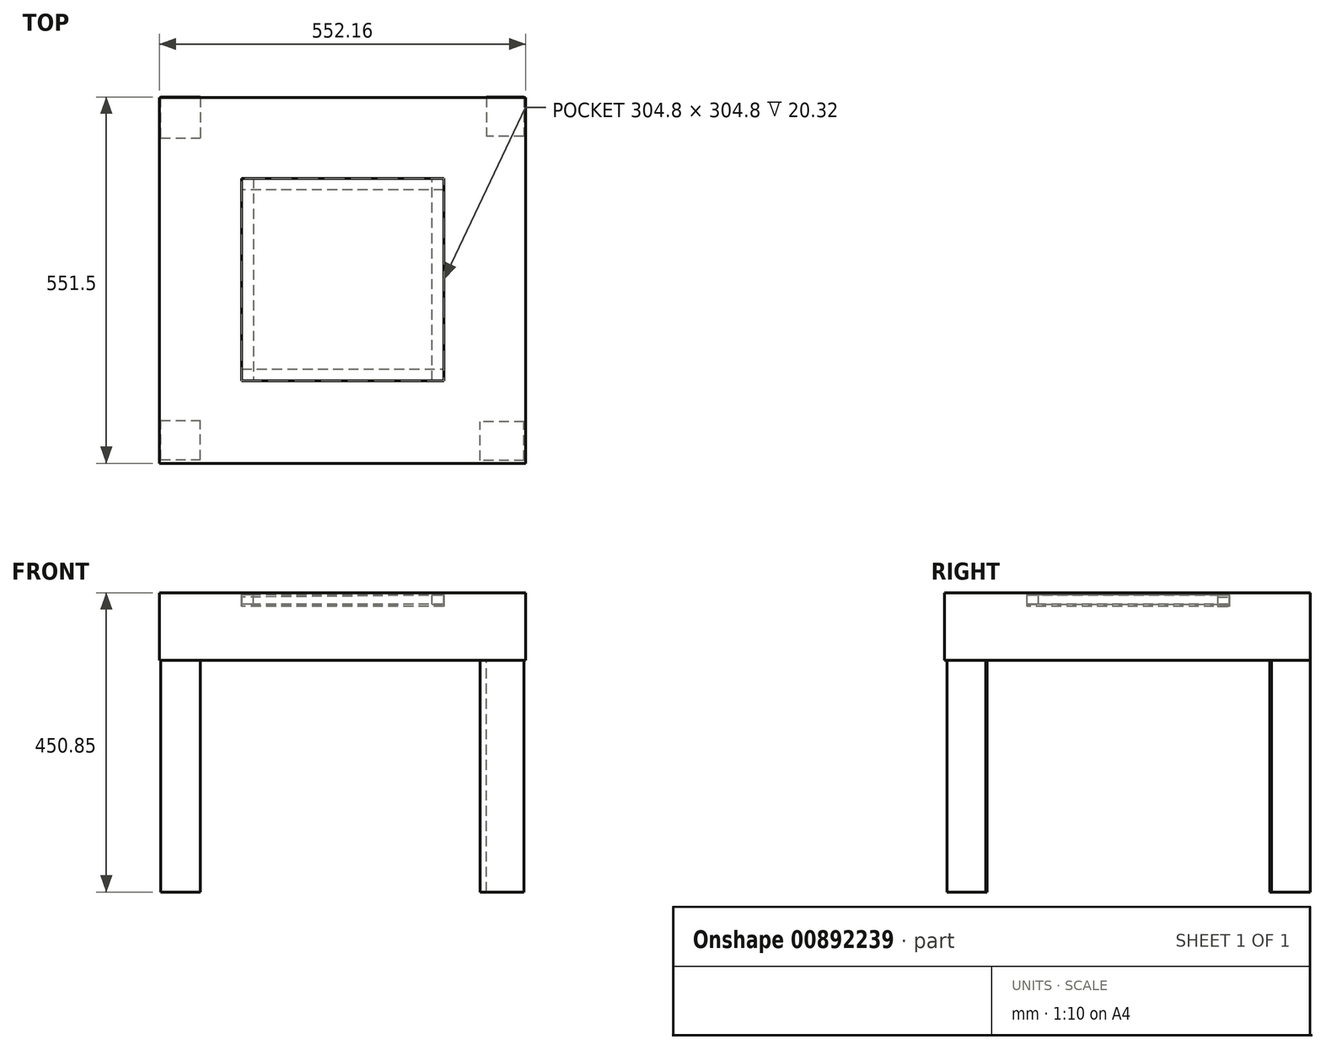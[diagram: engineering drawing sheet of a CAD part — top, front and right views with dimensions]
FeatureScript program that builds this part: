
annotation { "Feature Type Name" : "Feature", "Feature Type Description" : "" }
export const myFeature = defineFeature(function(context is Context, id is Id, definition is map)
    precondition{}
    {
        {
            var Q0;
            Q0=qCreatedBy(makeId("Top.planeOp"),FACE);
            var sketch = newSketch(context, id + "F0", { "sketchPlane" : qUnion([Q0])});
            skLineSegment(sketch, "E0.bottom", {"start": v(274.64, -274.64) * mm, "end": v(-274.64, -274.64) * mm});
            skLineSegment(sketch, "E0.top", {"start": v(274.64, 274.64) * mm, "end": v(-274.64, 274.64) * mm});
            skLineSegment(sketch, "E0.left", {"start": v(274.64, -274.64) * mm, "end": v(274.64, 274.64) * mm});
            skLineSegment(sketch, "E0.right", {"start": v(-274.64, -274.64) * mm, "end": v(-274.64, 274.64) * mm});
            skPoint(sketch, "E0.middle", {"position": v(0, 0) * mm});
            skSolve(sketch);
        }
        {
            var Q0;
            Q0=qCreatedBy(makeId("Front.planeOp"),FACE);
            var sketch = newSketch(context, id + "F1", { "sketchPlane" : qUnion([Q0])});
            skLineSegment(sketch, "E1.bottom", {"start": v(-276.39, 0) * mm, "end": v(275.77, 0) * mm});
            skLineSegment(sketch, "E1.top", {"start": v(-276.39, 101.6) * mm, "end": v(275.77, 101.6) * mm});
            skLineSegment(sketch, "E1.left", {"start": v(-276.39, 0) * mm, "end": v(-276.39, 101.6) * mm});
            skLineSegment(sketch, "E1.right", {"start": v(275.77, 0) * mm, "end": v(275.77, 101.6) * mm});
            skSolve(sketch);
        }
        {
            var Q0;
            Q0 = qSketchRegion(id + "F1", true);
            extrude(context, id + "F2", {"entities" : qUnion([Q0]), "depth" : 276.86 * mm, "offsetDistance" : 25.4 * mm});
        }
        {
            var Q0;
            Q0=makeQuery(id+"F1.imprint","IMPRINT",FACE,{"disambiguationData":[TD([[makeQuery(id+"F1.imprint","IMPRINT",EDGE,{"derivedFrom":sQuery(id+"F1.wireOp",EDGE,"E1.bottom")}),1.0]])]});
            extrude(context, id + "F3", {"entities" : qUnion([Q0]), "oppositeDirection" : true, "depth" : 274.32 * mm, "offsetDistance" : 25.4 * mm});
        }
        {
            var Q0;
            Q0=makeQuery(id+"F3.opExtrude","SWEPT_FACE",FACE,{"disambiguationData":[OSD([sQuery(id+"F1.wireOp",EDGE,"E1.top")])]});
            var sketch = newSketch(context, id + "F4", { "sketchPlane" : qUnion([Q0])});
            skLineSegment(sketch, "E2.bottom", {"start": v(152.4, 152.4) * mm, "end": v(-152.4, 152.4) * mm});
            skLineSegment(sketch, "E2.top", {"start": v(152.4, -152.4) * mm, "end": v(-152.4, -152.4) * mm});
            skLineSegment(sketch, "E2.left", {"start": v(152.4, 152.4) * mm, "end": v(152.4, -152.4) * mm});
            skLineSegment(sketch, "E2.right", {"start": v(-152.4, 152.4) * mm, "end": v(-152.4, -152.4) * mm});
            skPoint(sketch, "E2.middle", {"position": v(0, 0) * mm});
            skSolve(sketch);
        }
        {
            var Q0;
            Q0 = qSketchRegion(id + "F4", true);
            extrude(context, id + "F5", {"entities" : qUnion([Q0]), "operationType" : NewBodyOperationType.REMOVE, "oppositeDirection" : true, "depth" : 20.32 * mm, "offsetDistance" : 25.4 * mm});
        }
        {
            var Q0;
            Q0=makeQuery(id+"F2.opExtrude","SWEPT_BODY",BODY,{"disambiguationData":[OSD([sQuery(id+"F1.wireOp",EDGE,"E1.bottom"),sQuery(id+"F1.wireOp",EDGE,"E1.top"),sQuery(id+"F1.wireOp",EDGE,"E1.left"),sQuery(id+"F1.wireOp",EDGE,"E1.right")])]});
            var Q1;
            Q1=makeQuery(id+"F3.opExtrude","SWEPT_BODY",BODY,{"disambiguationData":[OSD([sQuery(id+"F1.wireOp",EDGE,"E1.bottom"),sQuery(id+"F1.wireOp",EDGE,"E1.top"),sQuery(id+"F1.wireOp",EDGE,"E1.left"),sQuery(id+"F1.wireOp",EDGE,"E1.right")])]});
            booleanBodies(context, id + "F6", {"operationType" : BooleanOperationType.UNION, "tools" : qUnion([Q0, Q1])});
        }
        {
            var Q0;
            {var subQ4=sQuery(id+"F4.wireOp",EDGE,"E2.top");var subQ5=sQuery(id+"F4.wireOp",EDGE,"E2.left");var subQ7=sQuery(id+"F4.wireOp",EDGE,"E2.right");var subQ9=sQuery(id+"F4.wireOp",EDGE,"E2.bottom");var subQ10=makeQuery(id+"F5.opExtrude","CAP_FACE",FACE,{"disambiguationData":[OSD([subQ9,subQ4,subQ5,subQ7])],"isStart":false});Q0=makeQuery(id+"F6.opBoolean","MERGE",FACE,{"derivedFrom":[makeQuery(id+"F5.boolean.opBoolean","COPY",FACE,{"disambiguationData":[TD([makeQuery(id+"F5.opExtrude","SWEPT_FACE",FACE,{"disambiguationData":[OSD([subQ9])]})])],"derivedFrom":subQ10}),makeQuery(id+"F5.boolean.opBoolean","COPY",FACE,{"disambiguationData":[TD([makeQuery(id+"F5.opExtrude","SWEPT_FACE",FACE,{"disambiguationData":[OSD([subQ4])]})])],"derivedFrom":subQ10})]});}
            var sketch = newSketch(context, id + "F7", { "sketchPlane" : qUnion([Q0])});
            skSolve(sketch);
        }
        {
            var Q0;
            {var subQ0=sQuery(id+"F4.wireOp",EDGE,"E2.bottom");Q0=makeQuery(id+"F7.imprint","IMPRINT",FACE,{"disambiguationData":[TD([[makeQuery(id+"F7.imprint","IMPRINT",EDGE,{"derivedFrom":makeQuery(id+"F5.boolean.opBoolean","COPY",EDGE,{"derivedFrom":makeQuery(id+"F5.opExtrude","CAP_EDGE",EDGE,{"disambiguationData":[OSD([subQ0])],"isStart":false})})}),1.0]])]});}
            var Q1;
            Q1 = qSketchRegion(id + "FyacHaDvZsvp2Am_1", true);
            extrude(context, id + "F8", {"entities" : qUnion([Q0, Q1]), "depth" : 3.07 * mm, "offsetDistance" : 25.4 * mm});
        }
        {
            var Q0;
            Q0=makeQuery(id+"F5.boolean.opBoolean","COPY",FACE,{"derivedFrom":makeQuery(id+"F5.opExtrude","SWEPT_FACE",FACE,{"disambiguationData":[OSD([sQuery(id+"F4.wireOp",EDGE,"E2.bottom")])]})});
            var sketch = newSketch(context, id + "F9", { "sketchPlane" : qUnion([Q0])});
            skLineSegment(sketch, "E3", {"start": v(-17.3, 101.6) * mm, "end": v(-17.3, 97.92) * mm});
            skLineSegment(sketch, "E4.bottom", {"start": v(152.4, 97.92) * mm, "end": v(-152.54, 94.84) * mm});
            skLineSegment(sketch, "E4.top", {"start": v(152.54, 84.35) * mm, "end": v(-152.4, 81.28) * mm});
            skLineSegment(sketch, "E4.left", {"start": v(152.4, 97.92) * mm, "end": v(152.54, 84.35) * mm});
            skLineSegment(sketch, "E4.right", {"start": v(-152.54, 94.84) * mm, "end": v(-152.4, 81.28) * mm});
            skSolve(sketch);
        }
        {
            var Q0;
            Q0 = qSketchRegion(id + "F9", true);
            extrude(context, id + "F10", {"entities" : qUnion([Q0]), "depth" : 17.54 * mm, "offsetDistance" : 25.4 * mm});
        }
        {
            var Q0;
            {var subQ2=sQuery(id+"F1.wireOp",EDGE,"E1.top");var subQ5=sQuery(id+"F4.wireOp",EDGE,"E2.left");var subQ8=makeQuery(id+"F5.opExtrude","SWEPT_FACE",FACE,{"disambiguationData":[OSD([subQ5])]});Q0=makeQuery(id+"F6.opBoolean","MERGE",FACE,{"derivedFrom":[makeQuery(id+"F5.boolean.opBoolean","COPY",FACE,{"disambiguationData":[TD([makeQuery(id+"F3.opExtrude","SWEPT_FACE",FACE,{"disambiguationData":[OSD([subQ2])]})])],"derivedFrom":subQ8}),makeQuery(id+"F5.boolean.opBoolean","COPY",FACE,{"disambiguationData":[TD([makeQuery(id+"F2.opExtrude","SWEPT_FACE",FACE,{"disambiguationData":[OSD([subQ2])]})])],"derivedFrom":subQ8})]});}
            var sketch = newSketch(context, id + "F11", { "sketchPlane" : qUnion([Q0])});
            skLineSegment(sketch, "E5", {"start": v(0, 101.6) * mm, "end": v(-0.3, 97.93) * mm});
            skLineSegment(sketch, "E6.bottom", {"start": v(152.4, 97.93) * mm, "end": v(-152.4, 97.93) * mm});
            skLineSegment(sketch, "E6.top", {"start": v(152.4, 84.37) * mm, "end": v(-152.4, 84.37) * mm});
            skLineSegment(sketch, "E6.left", {"start": v(152.4, 97.93) * mm, "end": v(152.4, 84.37) * mm});
            skLineSegment(sketch, "E6.right", {"start": v(-152.4, 97.93) * mm, "end": v(-152.4, 84.37) * mm});
            skSolve(sketch);
        }
        {
            var Q0;
            Q0 = qSketchRegion(id + "F11", true);
            extrude(context, id + "F12", {"entities" : qUnion([Q0]), "depth" : 17.54 * mm, "offsetDistance" : 25.4 * mm});
        }
        {
            var Q0;
            Q0=makeQuery(id+"F5.boolean.opBoolean","COPY",FACE,{"derivedFrom":makeQuery(id+"F5.opExtrude","SWEPT_FACE",FACE,{"disambiguationData":[OSD([sQuery(id+"F4.wireOp",EDGE,"E2.top")])]})});
            var sketch = newSketch(context, id + "F13", { "sketchPlane" : qUnion([Q0])});
            skLineSegment(sketch, "E7", {"start": v(0, 101.6) * mm, "end": v(0, 97.92) * mm});
            skLineSegment(sketch, "E8.bottom", {"start": v(152.4, 97.92) * mm, "end": v(-152.4, 97.92) * mm});
            skLineSegment(sketch, "E8.top", {"start": v(152.4, 84.35) * mm, "end": v(-152.4, 84.35) * mm});
            skLineSegment(sketch, "E8.left", {"start": v(152.4, 97.92) * mm, "end": v(152.4, 84.35) * mm});
            skLineSegment(sketch, "E8.right", {"start": v(-152.4, 97.92) * mm, "end": v(-152.4, 84.35) * mm});
            skSolve(sketch);
        }
        {
            var Q0;
            Q0 = qSketchRegion(id + "F13", true);
            extrude(context, id + "F14", {"entities" : qUnion([Q0]), "depth" : 17.54 * mm, "offsetDistance" : 25.4 * mm});
        }
        {
            var Q0;
            {var subQ2=sQuery(id+"F1.wireOp",EDGE,"E1.top");var subQ5=sQuery(id+"F4.wireOp",EDGE,"E2.right");var subQ8=makeQuery(id+"F5.opExtrude","SWEPT_FACE",FACE,{"disambiguationData":[OSD([subQ5])]});Q0=makeQuery(id+"F6.opBoolean","MERGE",FACE,{"derivedFrom":[makeQuery(id+"F5.boolean.opBoolean","COPY",FACE,{"disambiguationData":[TD([makeQuery(id+"F3.opExtrude","SWEPT_FACE",FACE,{"disambiguationData":[OSD([subQ2])]})])],"derivedFrom":subQ8}),makeQuery(id+"F5.boolean.opBoolean","COPY",FACE,{"disambiguationData":[TD([makeQuery(id+"F2.opExtrude","SWEPT_FACE",FACE,{"disambiguationData":[OSD([subQ2])]})])],"derivedFrom":subQ8})]});}
            var sketch = newSketch(context, id + "F15", { "sketchPlane" : qUnion([Q0])});
            skLineSegment(sketch, "E9", {"start": v(0, 101.6) * mm, "end": v(0, 97.92) * mm});
            skPoint(sketch, "E9.endSnap0", {"position": v(0, 81.28) * mm});
            skLineSegment(sketch, "E10.bottom", {"start": v(152.4, 97.92) * mm, "end": v(-152.4, 97.92) * mm});
            skLineSegment(sketch, "E10.top", {"start": v(143.8, 84.35) * mm, "end": v(-152.4, 84.35) * mm});
            skLineSegment(sketch, "E10.left", {"start": v(152.4, 97.92) * mm, "end": v(152.4, 84.35) * mm});
            skLineSegment(sketch, "E10.right", {"start": v(-152.4, 97.92) * mm, "end": v(-152.4, 84.35) * mm});
            skLineSegment(sketch, "E11", {"start": v(143.8, 84.35) * mm, "end": v(152.4, 84.35) * mm});
            skLineSegment(sketch, "E12", {"start": v(152.4, 84.35) * mm, "end": v(152.4, 97.92) * mm});
            skSolve(sketch);
        }
        {
            var Q0;
            Q0 = qSketchRegion(id + "F15", true);
            extrude(context, id + "F16", {"entities" : qUnion([Q0]), "depth" : 17.54 * mm, "offsetDistance" : 25.4 * mm});
        }
        {
            var Q0;
            {var subQ1=sQuery(id+"F15.wireOp",EDGE,"E10.left");Q0=makeQuery(id+"F15.imprint","IMPRINT",FACE,{"disambiguationData":[TD([[makeQuery(id+"F15.imprint","IMPRINT",EDGE,{"derivedFrom":subQ1}),1.0]])]});}
            extrude(context, id + "F17", {"entities" : qUnion([Q0]), "depth" : 17.54 * mm, "offsetDistance" : 25.4 * mm});
        }
        {
            var Q0;
            {var subQ0=sQuery(id+"F15.wireOp",EDGE,"E9");Q0=makeQuery(id+"F15.imprint","IMPRINT",FACE,{"disambiguationData":[TD([[makeQuery(id+"F15.imprint","IMPRINT",EDGE,{"derivedFrom":subQ0}),1.0]])]});}
            var Q1;
            {var subQ0=sQuery(id+"F15.wireOp",EDGE,"E9");Q1=makeQuery(id+"F15.imprint","IMPRINT",FACE,{"disambiguationData":[TD([[makeQuery(id+"F15.imprint","IMPRINT",EDGE,{"derivedFrom":subQ0}),-1.0]])]});}
            extrude(context, id + "F18", {"entities" : qUnion([Q0, Q1]), "depth" : 304.8 * mm, "offsetDistance" : 25.4 * mm});
        }
        {
            var Q0;
            Q0=makeQuery(id+"F0.imprint","IMPRINT",FACE,{"disambiguationData":[TD([[makeQuery(id+"F0.imprint","IMPRINT",EDGE,{"derivedFrom":sQuery(id+"F0.wireOp",EDGE,"E0.bottom")}),-1.0]])]});
            var sketch = newSketch(context, id + "F19", { "sketchPlane" : qUnion([Q0])});
            skLineSegment(sketch, "E13.bottom", {"start": v(-277.7, -271.61) * mm, "end": v(-214.55, -271.61) * mm});
            skLineSegment(sketch, "E13.top", {"start": v(-277.7, -212.67) * mm, "end": v(-214.55, -212.67) * mm});
            skLineSegment(sketch, "E13.left", {"start": v(-277.7, -271.61) * mm, "end": v(-277.7, -212.67) * mm});
            skLineSegment(sketch, "E13.right", {"start": v(-214.55, -271.61) * mm, "end": v(-214.55, -212.67) * mm});
            skLineSegment(sketch, "E14.bottom", {"start": v(274.65, -273.34) * mm, "end": v(216.57, -273.34) * mm});
            skLineSegment(sketch, "E14.top", {"start": v(274.65, -212.67) * mm, "end": v(216.57, -212.67) * mm});
            skLineSegment(sketch, "E14.left", {"start": v(274.65, -273.34) * mm, "end": v(274.65, -212.67) * mm});
            skLineSegment(sketch, "E14.right", {"start": v(216.57, -273.34) * mm, "end": v(216.57, -212.67) * mm});
            skLineSegment(sketch, "E15.bottom", {"start": v(273.1, 276.5) * mm, "end": v(216.57, 276.5) * mm});
            skLineSegment(sketch, "E15.top", {"start": v(273.1, 215.91) * mm, "end": v(216.57, 215.91) * mm});
            skLineSegment(sketch, "E15.left", {"start": v(273.1, 276.5) * mm, "end": v(273.1, 215.91) * mm});
            skLineSegment(sketch, "E15.right", {"start": v(216.57, 276.5) * mm, "end": v(216.57, 215.91) * mm});
            skLineSegment(sketch, "E16.bottom", {"start": v(-278.43, 275.25) * mm, "end": v(-214.55, 275.25) * mm});
            skLineSegment(sketch, "E16.top", {"start": v(-278.43, 213.34) * mm, "end": v(-214.55, 213.34) * mm});
            skLineSegment(sketch, "E16.left", {"start": v(-278.43, 275.25) * mm, "end": v(-278.43, 213.34) * mm});
            skLineSegment(sketch, "E16.right", {"start": v(-214.55, 275.25) * mm, "end": v(-214.55, 213.34) * mm});
            skSolve(sketch);
        }
        {
            var Q0;
            {var subQ0=sQuery(id+"F19.wireOp",EDGE,"E13.right");Q0=makeQuery(id+"F19.imprint","IMPRINT",FACE,{"disambiguationData":[TD([[makeQuery(id+"F19.imprint","IMPRINT",EDGE,{"derivedFrom":subQ0}),1.0]])]});}
            var Q1;
            {var subQ0=sQuery(id+"F19.wireOp",EDGE,"E15.top");Q1=makeQuery(id+"F19.imprint","IMPRINT",FACE,{"disambiguationData":[TD([[makeQuery(id+"F19.imprint","IMPRINT",EDGE,{"derivedFrom":subQ0}),-1.0]])]});}
            var Q2;
            {var subQ0=sQuery(id+"F19.wireOp",EDGE,"E16.right");var subQ1=sQuery(id+"F19.wireOp",EDGE,"E16.top");var subQ2=makeQuery(id+"F19.imprint","INTERSECT",VERTEX,{"derivedFrom":[subQ1,subQ0]});Q2=makeQuery(id+"F19.imprint","IMPRINT",FACE,{"disambiguationData":[TD([[makeQuery(id+"F19.imprint","IMPRINT",EDGE,{"disambiguationData":[TD([[subQ2,1.0]])],"derivedFrom":subQ1}),1.0]])]});}
            extrude(context, id + "F20", {"entities" : qUnion([Q0, Q1, Q2]), "operationType" : NewBodyOperationType.ADD, "oppositeDirection" : true, "depth" : 349.25 * mm, "offsetDistance" : 25.4 * mm});
        }
        {
            var Q0;
            Q0=makeQuery(id+"F0.imprint","IMPRINT",FACE,{"disambiguationData":[TD([[makeQuery(id+"F0.imprint","IMPRINT",EDGE,{"derivedFrom":sQuery(id+"F0.wireOp",EDGE,"E0.bottom")}),-1.0]])]});
            var sketch = newSketch(context, id + "F21", { "sketchPlane" : qUnion([Q0])});
            skLineSegment(sketch, "E17.bottom", {"start": v(273.27, -272.54) * mm, "end": v(207.03, -272.54) * mm});
            skLineSegment(sketch, "E17.top", {"start": v(273.27, -214.4) * mm, "end": v(207.03, -214.4) * mm});
            skLineSegment(sketch, "E17.left", {"start": v(273.27, -272.54) * mm, "end": v(273.27, -214.4) * mm});
            skLineSegment(sketch, "E17.right", {"start": v(207.03, -272.54) * mm, "end": v(207.03, -214.4) * mm});
            skSolve(sketch);
        }
        {
            var Q0;
            Q0 = qSketchRegion(id + "F21", true);
            extrude(context, id + "F22", {"entities" : qUnion([Q0]), "operationType" : NewBodyOperationType.ADD, "oppositeDirection" : true, "depth" : 349.25 * mm, "offsetDistance" : 25.4 * mm});
        }
    });
